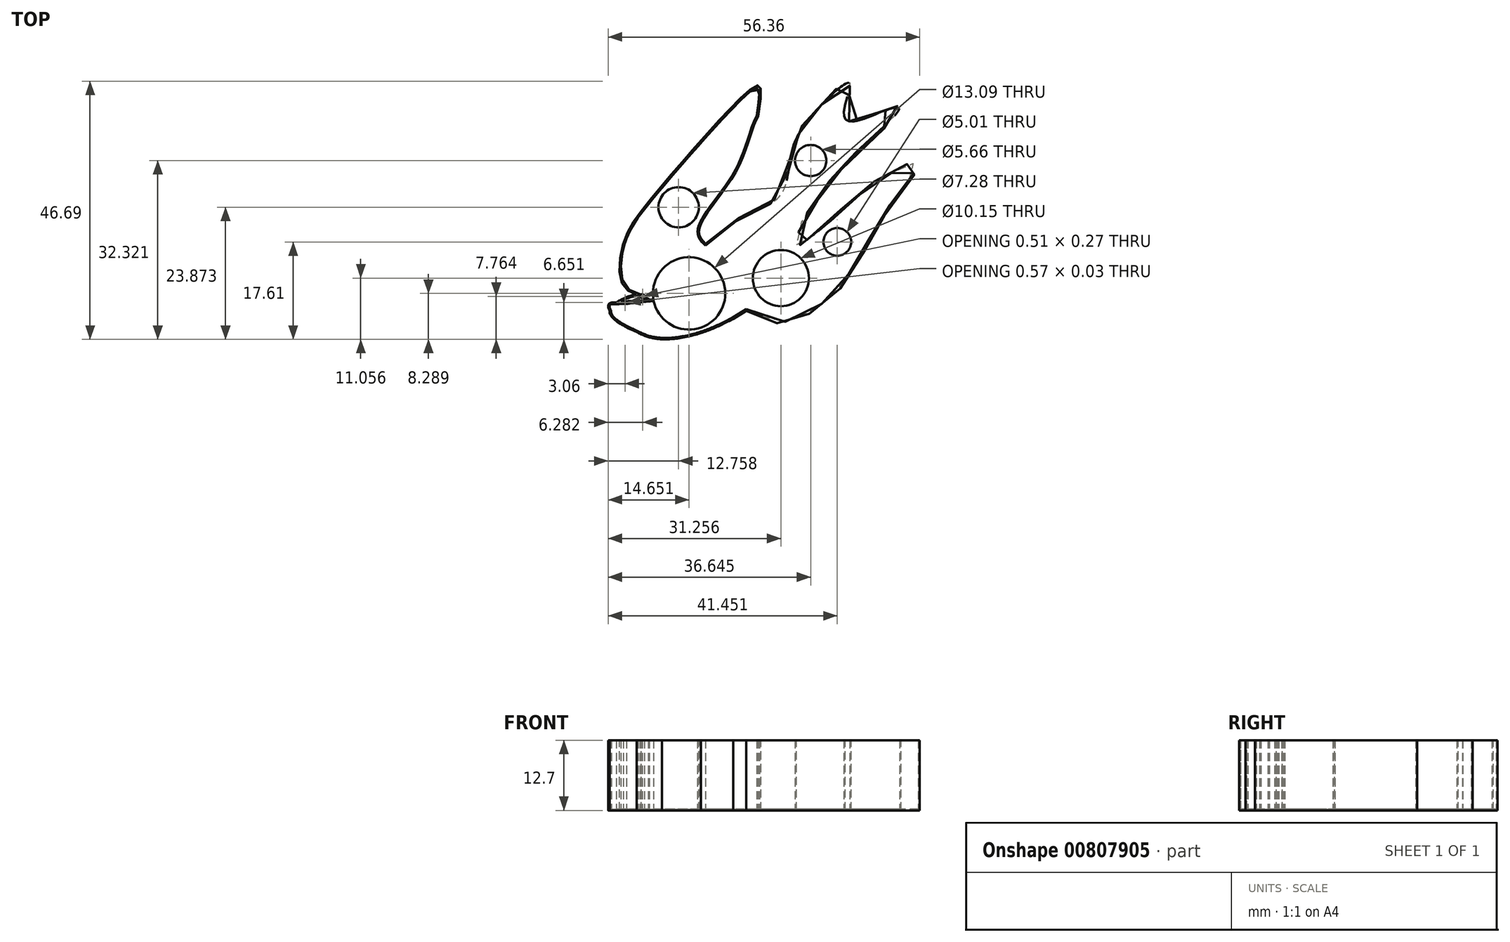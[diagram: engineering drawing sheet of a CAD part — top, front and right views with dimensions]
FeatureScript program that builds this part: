
annotation { "Feature Type Name" : "Feature", "Feature Type Description" : "" }
export const myFeature = defineFeature(function(context is Context, id is Id, definition is map)
    precondition{}
    {
        {
            var Q0;
            Q0=qCreatedBy(makeId("Top.planeOp"),FACE);
            var sketch = newSketch(context, id + "F0", { "sketchPlane" : qUnion([Q0])});
            skFitSpline(sketch, "E0", {"points": [v(-20.58, -12.12) * mm, v(-24.3, -10.16) * mm, v(-24.4, -2.49) * mm, v(-20.2, 4.63) * mm, v(-11.84, 14.46) * mm, v(-5.76, 21.16) * mm, v(0, 26.17) * mm, v(0, 20.59) * mm], "startDerivative": vector(-39.64, 13.42) * mm, "endDerivative": vector(-13.6, -88.5) * mm});
            skFitSpline(sketch, "E1", {"points": [v(0, 20.59) * mm, v(-3.94, 10.66) * mm, v(-10.67, 0) * mm, v(-9.5, -2.46) * mm], "startDerivative": vector(-9.12, -14.62) * mm, "endDerivative": vector(9.42, -8.4) * mm});
            skFitSpline(sketch, "E2", {"points": [v(-9.5, -2.46) * mm, v(-2.48, 2.77) * mm, v(3.95, 6.57) * mm, v(5.81, 14.15) * mm, v(11.1, 22.66) * mm, v(16.8, 26.74) * mm, v(15.93, 20.3) * mm, v(23.12, 21.94) * mm, v(25.87, 22.06) * mm, v(16.96, 12.97) * mm, v(11.1, 5.93) * mm, v(7.45, 0) * mm, v(7.16, -2.46) * mm, v(10.96, 0) * mm, v(19.14, 7.4) * mm, v(25.04, 11.07) * mm, v(29.2, 12.23) * mm, v(24.4, 4.82) * mm, v(19.94, -2.46) * mm, v(14.47, -10.97) * mm, v(8.33, -15.64) * mm, v(3.07, -16.81) * mm, v(-2.1, -14.58) * mm], "startDerivative": vector(131.76, 110.26) * mm, "endDerivative": vector(-136.68, 49.94) * mm});
            skFitSpline(sketch, "E3", {"points": [v(-2.1, -14.58) * mm, v(-10.35, -18.63) * mm, v(-17.39, -19.74) * mm, v(-21.98, -18.44) * mm, v(-26.85, -14.58) * mm, v(-21.98, -11.65) * mm, v(-20.58, -12.12) * mm], "startDerivative": vector(-32.87, -20.4) * mm, "endDerivative": vector(11.24, -9.83) * mm});
            skFitSpline(sketch, "E4", {"points": [v(-4.48, -16.06) * mm, v(-10.35, -18.63) * mm, v(-17.39, -19.74) * mm, v(-21.98, -18.44) * mm, v(-26.85, -14.58) * mm, v(-26.85, -13.24) * mm, v(-23.77, -13.08) * mm, v(-20.9, -11.84) * mm], "startDerivative": vector(-31.8, -16.23) * mm, "endDerivative": vector(21.33, 13.9) * mm});
            skFitSpline(sketch, "E5", {"points": [v(-26.85, -13.24) * mm, v(-23.77, -13.08) * mm], "startDerivative": vector(3.08, 0.16) * mm, "endDerivative": vector(3.08, 0.16) * mm});
            skLineSegment(sketch, "E6", {"start": v(-4.48, -16.06) * mm, "end": v(-2.1, -14.58) * mm});
            skSolve(sketch);
        }
        {
            var Q0;
            Q0 = qSketchRegion(id + "F0", true);
            extrude(context, id + "F1", {"entities" : qUnion([Q0]), "depth" : 12.7 * mm, "offsetDistance" : 25.4 * mm});
        }
        {
            var Q0;
            Q0=makeQuery(id+"F1.opExtrude","CAP_FACE",FACE,{"disambiguationData":[OSD([sQuery(id+"F0.wireOp",EDGE,"E0"),sQuery(id+"F0.wireOp",EDGE,"E1"),sQuery(id+"F0.wireOp",EDGE,"E2"),sQuery(id+"F0.wireOp",EDGE,"E3"),sQuery(id+"F0.wireOp",EDGE,"E4"),sQuery(id+"F0.wireOp",EDGE,"E5"),sQuery(id+"F0.wireOp",EDGE,"E6")])],"isStart":false});
            shell(context, id + "F2", {"entities" : qUnion([Q0]), "thickness" : 0.25 * mm});
        }
        {
            var Q0;
            Q0=makeQuery(id+"F1.opExtrude","CAP_FACE",FACE,{"disambiguationData":[OSD([sQuery(id+"F0.wireOp",EDGE,"E0"),sQuery(id+"F0.wireOp",EDGE,"E1"),sQuery(id+"F0.wireOp",EDGE,"E2"),sQuery(id+"F0.wireOp",EDGE,"E3"),sQuery(id+"F0.wireOp",EDGE,"E4"),sQuery(id+"F0.wireOp",EDGE,"E5"),sQuery(id+"F0.wireOp",EDGE,"E6")])],"isStart":true});
            var sketch = newSketch(context, id + "F3", { "sketchPlane" : qUnion([Q0])});
            skCircle(sketch, "E7", {"center": v(-12.47, 11.46) * mm, "radius": 6.55 * mm});
            skCircle(sketch, "E8", {"center": v(4.14, 8.7) * mm, "radius": 5.07 * mm});
            skCircle(sketch, "E9", {"center": v(-14.36, -4.12) * mm, "radius": 3.64 * mm});
            skCircle(sketch, "E10", {"center": v(9.52, -12.57) * mm, "radius": 2.83 * mm});
            skCircle(sketch, "E11", {"center": v(14.33, 2.14) * mm, "radius": 2.5 * mm});
            skSolve(sketch);
        }
        {
            var Q0;
            Q0 = qSketchRegion(id + "F3", true);
            extrude(context, id + "F4", {"entities" : qUnion([Q0]), "operationType" : NewBodyOperationType.REMOVE, "oppositeDirection" : true, "depth" : 25.4 * mm, "offsetDistance" : 25.4 * mm});
        }
    });
